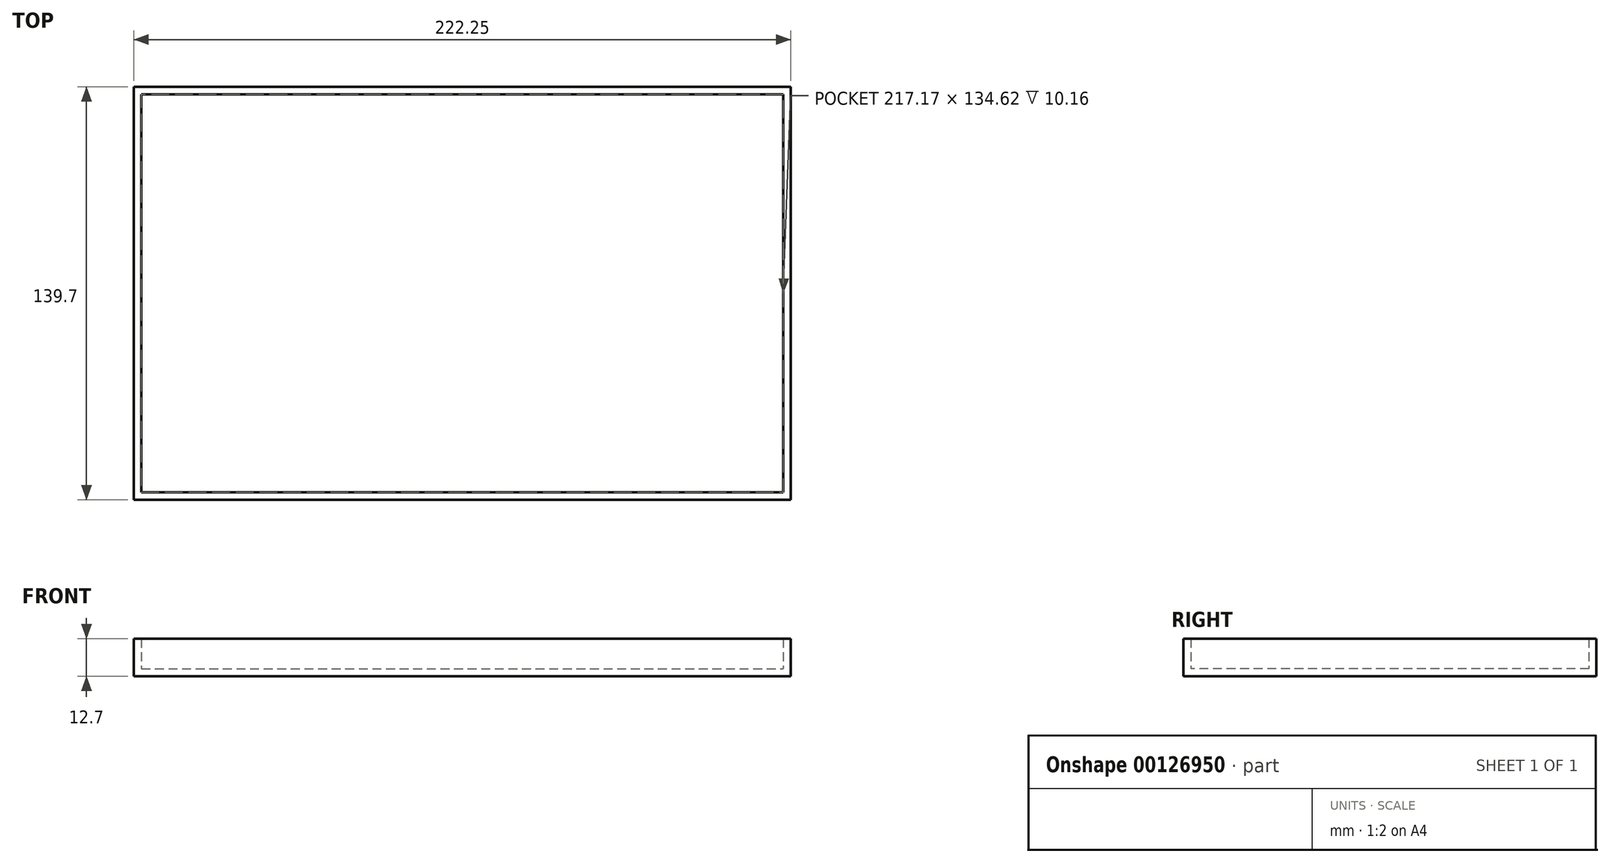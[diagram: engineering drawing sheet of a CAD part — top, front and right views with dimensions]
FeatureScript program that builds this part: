
annotation { "Feature Type Name" : "Feature", "Feature Type Description" : "" }
export const myFeature = defineFeature(function(context is Context, id is Id, definition is map)
    precondition{}
    {
        {
            var Q0;
            Q0=qCreatedBy(makeId("Top.planeOp"),FACE);
            var sketch = newSketch(context, id + "F0", { "sketchPlane" : qUnion([Q0])});
            skLineSegment(sketch, "E0.bottom", {"start": v(-109.34, 37.92) * mm, "end": v(112.9, 37.92) * mm});
            skLineSegment(sketch, "E0.top", {"start": v(-109.34, -101.78) * mm, "end": v(112.9, -101.78) * mm});
            skLineSegment(sketch, "E0.left", {"start": v(-109.34, 37.92) * mm, "end": v(-109.34, -101.78) * mm});
            skLineSegment(sketch, "E0.right", {"start": v(112.9, 37.92) * mm, "end": v(112.9, -101.78) * mm});
            skSolve(sketch);
        }
        {
            var Q0;
            Q0 = qSketchRegion(id + "F0", true);
            extrude(context, id + "F1", {"entities" : qUnion([Q0]), "depth" : 12.7 * mm});
        }
        {
            var Q0;
            Q0 = qSketchRegion(id + "F0", true);
            extrude(context, id + "F2", {"entities" : qUnion([Q0]), "operationType" : NewBodyOperationType.ADD, "depth" : 12.7 * mm});
        }
        {
            var Q0;
            Q0=makeQuery(id+"F1.opExtrude","CAP_FACE",FACE,{"disambiguationData":[OSD([sQuery(id+"F0.wireOp",EDGE,"E0.bottom"),sQuery(id+"F0.wireOp",EDGE,"E0.top"),sQuery(id+"F0.wireOp",EDGE,"E0.left"),sQuery(id+"F0.wireOp",EDGE,"E0.right")])],"isStart":false});
            shell(context, id + "F3", {"entities" : qUnion([Q0]), "thickness" : 2.54 * mm});
        }
    });
